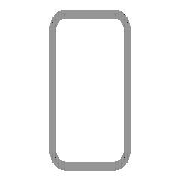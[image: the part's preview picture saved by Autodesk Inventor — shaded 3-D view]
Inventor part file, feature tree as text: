
AUTODESK INVENTOR PART (.ipt)
format: ipt  version: 2025 (Build 290162010, 162A)  size: 134,656 bytes
history: native  units: mm (DEFAULTED — no unit token found)
features: other x4, sketch x1, plane x1
ambient origin geometry x8: Origin, YZ Plane, XZ Plane, XY Plane, X Axis, Y Axis, Z Axis, Center Point
bodies: Solid1 (feature_tree), Body (feature_tree)
feature tree (6):
  parser-record x1  (decoder bookkeeping rows leaked as tree rows — omitted from the tree; the rows remain in map.json)
  other  "Driven Length"
  other  "Start Plane"
  other  "End Plane"
  sketch  "Sketch3"  dims[d3=1170.0mm d4=0.0mm d7=4.0mm d9=40.0mm d11=80.0mm d12=2.0mm d13=40.0mm d14=1210.0mm d15=20.0mm d16=40.0mm d17=90.0deg d18=1170.0mm]
  plane  "Work Plane3"
